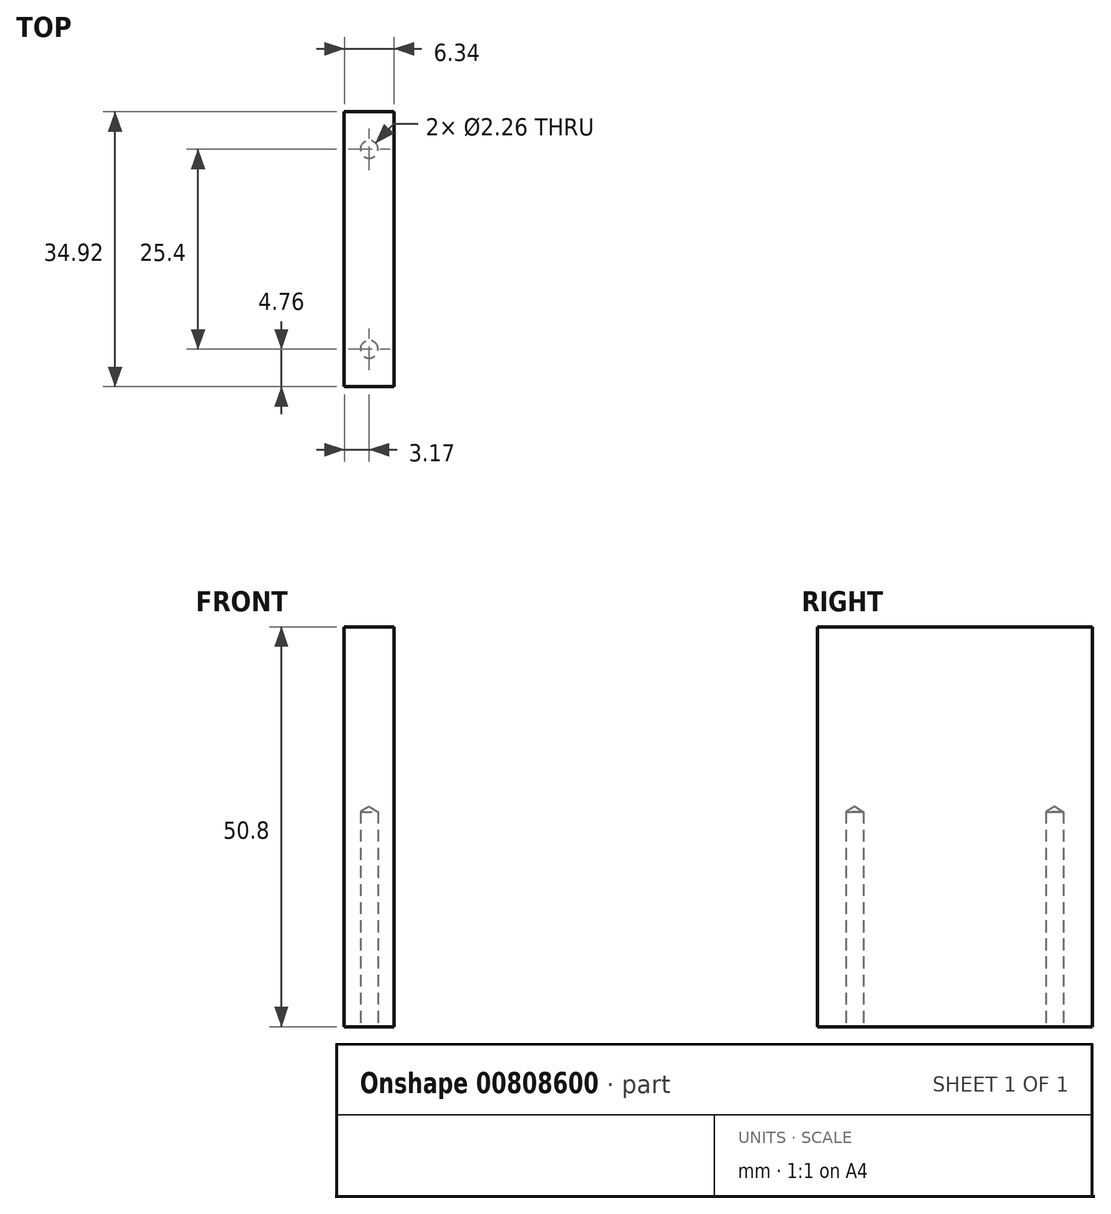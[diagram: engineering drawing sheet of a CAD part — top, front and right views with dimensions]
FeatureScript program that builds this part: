
annotation { "Feature Type Name" : "Feature", "Feature Type Description" : "" }
export const myFeature = defineFeature(function(context is Context, id is Id, definition is map)
    precondition{}
    {
        {
            var Q0;
            Q0=qCreatedBy(makeId("Right.planeOp"),FACE);
            var sketch = newSketch(context, id + "F0", { "sketchPlane" : qUnion([Q0])});
            skLineSegment(sketch, "E0.bottom", {"start": v(-17.46, 25.4) * mm, "end": v(17.46, 25.4) * mm});
            skLineSegment(sketch, "E0.top", {"start": v(-17.46, -25.4) * mm, "end": v(17.46, -25.4) * mm});
            skLineSegment(sketch, "E0.left", {"start": v(-17.46, 25.4) * mm, "end": v(-17.46, -25.4) * mm});
            skLineSegment(sketch, "E0.right", {"start": v(17.46, 25.4) * mm, "end": v(17.46, -25.4) * mm});
            skLineSegment(sketch, "E1", {"start": v(-17.46, -25.4) * mm, "end": v(17.46, 25.4) * mm, "construction": true});
            skSolve(sketch);
        }
        {
            var Q0;
            Q0 = qSketchRegion(id + "F0", true);
            extrude(context, id + "F1", {"entities" : qUnion([Q0]), "endBound" : BoundingType.SYMMETRIC, "depth" : 6.35 * mm, "offsetDistance" : 25.4 * mm});
        }
        {
            var Q0;
            Q0=makeQuery(id+"F1.opExtrude","SWEPT_FACE",FACE,{"disambiguationData":[OSD([sQuery(id+"F0.wireOp",EDGE,"E0.top")])]});
            var sketch = newSketch(context, id + "F2", { "sketchPlane" : qUnion([Q0])});
            skPoint(sketch, "E2", {"position": v(0, 12.7) * mm});
            skPoint(sketch, "E3", {"position": v(0, -12.7) * mm});
            skSolve(sketch);
        }
        {
            var Q0;
            Q0=sQuery(id+"F2.wireOp",VERTEX,"E2");
            var Q1;
            Q1=sQuery(id+"F2.wireOp",VERTEX,"E3");
            var Q2;
            Q2=makeQuery(id+"F1.opExtrude","SWEPT_BODY",BODY,{"disambiguationData":[OSD([sQuery(id+"F0.wireOp",EDGE,"E0.bottom"),sQuery(id+"F0.wireOp",EDGE,"E0.top"),sQuery(id+"F0.wireOp",EDGE,"E0.left"),sQuery(id+"F0.wireOp",EDGE,"E0.right")])]});
            hole(context, id + "F3", {"style" : HoleStyle.SIMPLE, "endStyle" : HoleEndStyle.BLIND, "standardTappedOrClearance" : lookupTablePath({ "standard" : "ANSI", "engagement" : "75%", "pitch" : "40 tpi", "size" : "#4", "type" : "Tapped" }), "standardBlindInLast" : lookupTablePath({ "standard" : "ANSI", "engagement" : "75%", "pitch" : "40 tpi", "size" : "#4", "type" : "Tapped" }), "holeDiameter" : 2.26 * mm, "majorDiameter" : 2.84 * mm, "showTappedDepth" : true, "holeDepth" : 27.3 * mm, "tappedDepth" : 25.4 * mm, "tapClearance" : 3, "locations" : qUnion([Q0, Q1]), "scope" : qUnion([Q2])});
        }
    });
